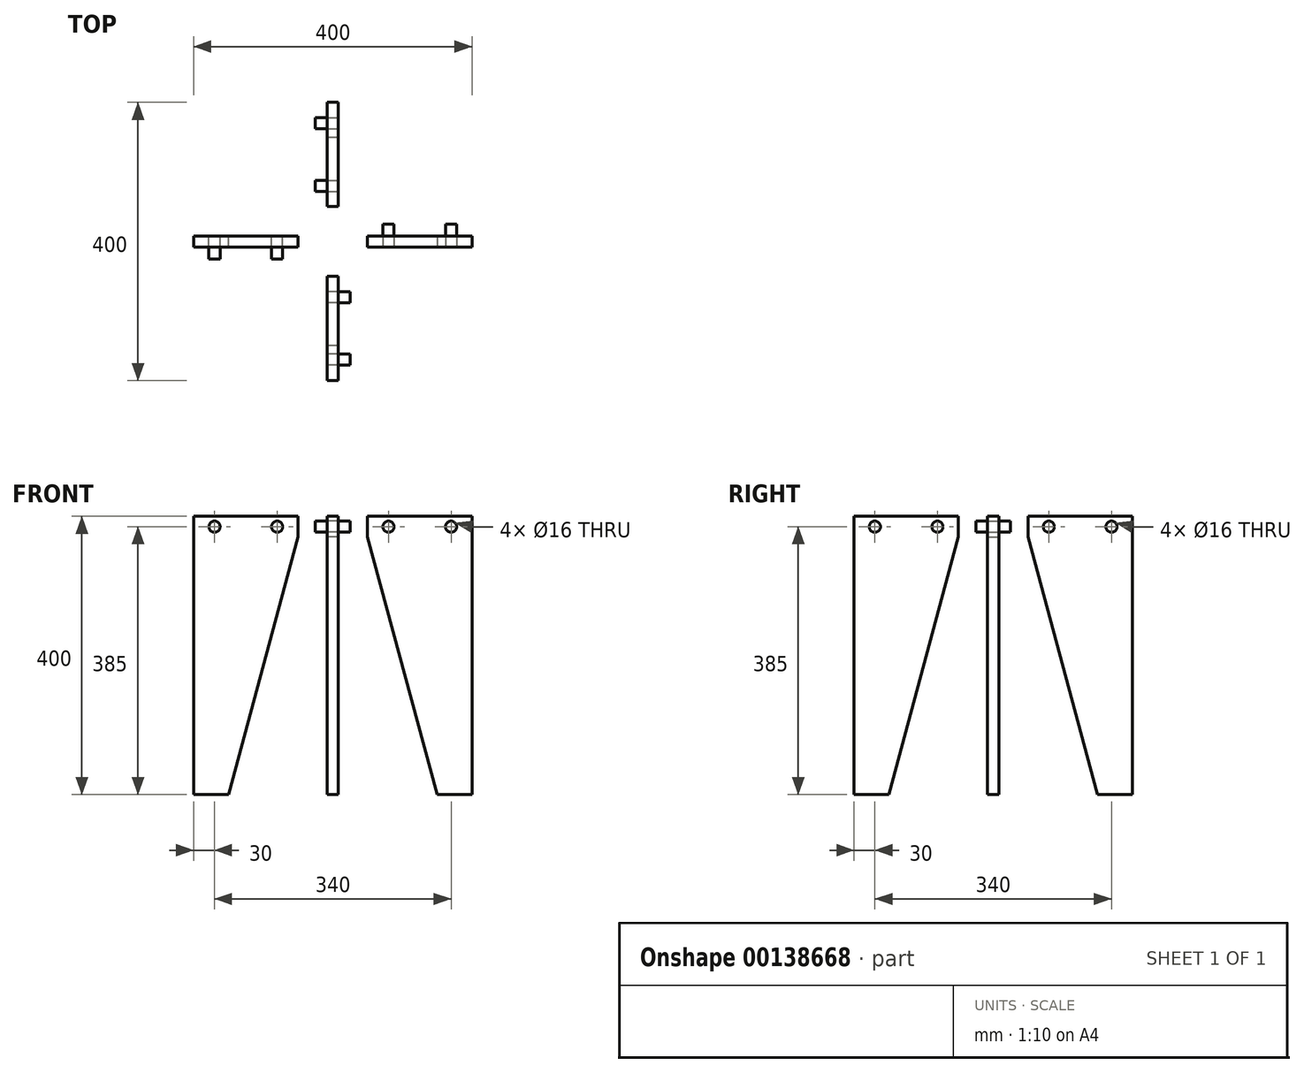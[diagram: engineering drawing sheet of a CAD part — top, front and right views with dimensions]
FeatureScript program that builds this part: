
annotation { "Feature Type Name" : "Feature", "Feature Type Description" : "" }
export const myFeature = defineFeature(function(context is Context, id is Id, definition is map)
    precondition{}
    {
        {
            var Q0;
            Q0=qCreatedBy(makeId("Front.planeOp"),FACE);
            var sketch = newSketch(context, id + "F0", { "sketchPlane" : qUnion([Q0])});
            skLineSegment(sketch, "E0", {"start": v(0, 0) * mm, "end": v(0, 319.28) * mm, "construction": true});
            skLineSegment(sketch, "E1", {"start": v(-50, 400) * mm, "end": v(-200, 400) * mm});
            skLineSegment(sketch, "E2", {"start": v(-200, 400) * mm, "end": v(-200, 0) * mm});
            skLineSegment(sketch, "E3", {"start": v(-200, 0) * mm, "end": v(-150, 0) * mm});
            skLineSegment(sketch, "E4.bottom", {"start": v(-250, 400) * mm, "end": v(0, 400) * mm, "construction": true});
            skLineSegment(sketch, "E4.top", {"start": v(-250, 370) * mm, "end": v(0, 370) * mm, "construction": true});
            skLineSegment(sketch, "E4.left", {"start": v(-250, 400) * mm, "end": v(-250, 370) * mm, "construction": true});
            skLineSegment(sketch, "E4.right", {"start": v(0, 400) * mm, "end": v(0, 370) * mm, "construction": true});
            skLineSegment(sketch, "E5", {"start": v(-50, 400) * mm, "end": v(-50, 370) * mm});
            skLineSegment(sketch, "E6", {"start": v(-50, 370) * mm, "end": v(-150, 0) * mm});
            skLineSegment(sketch, "E7", {"start": v(-80, 385) * mm, "end": v(-170, 385) * mm, "construction": true});
            skCircle(sketch, "E8", {"center": v(-80, 385) * mm, "radius": 8 * mm});
            skCircle(sketch, "E9", {"center": v(-170, 385) * mm, "radius": 8 * mm});
            skSolve(sketch);
        }
        {
            var Q0;
            {var subQ5=sQuery(id+"F0.wireOp",EDGE,"E5");Q0=makeQuery(id+"F0.imprint","IMPRINT",FACE,{"disambiguationData":[TD([[makeQuery(id+"F0.imprint","IMPRINT",EDGE,{"derivedFrom":subQ5}),-1.0]])]});}
            var Q1;
            {var subQ0=sQuery(id+"F0.wireOp",EDGE,"E3");Q1=makeQuery(id+"F0.imprint","IMPRINT",FACE,{"disambiguationData":[TD([[makeQuery(id+"F0.imprint","IMPRINT",EDGE,{"derivedFrom":subQ0}),1.0]])]});}
            extrude(context, id + "F1", {"entities" : qUnion([Q0, Q1]), "endBound" : BoundingType.SYMMETRIC, "depth" : 16 * mm});
        }
        {
            var Q0;
            Q0=makeQuery(id+"F0.imprint","IMPRINT",FACE,{"disambiguationData":[TD([[makeQuery(id+"F0.imprint","IMPRINT",EDGE,{"derivedFrom":sQuery(id+"F0.wireOp",EDGE,"E8")}),1.0]])]});
            var Q1;
            Q1=makeQuery(id+"F0.imprint","IMPRINT",FACE,{"disambiguationData":[TD([[makeQuery(id+"F0.imprint","IMPRINT",EDGE,{"derivedFrom":sQuery(id+"F0.wireOp",EDGE,"E9")}),1.0]])]});
            extrude(context, id + "F2", {"entities" : qUnion([Q0, Q1]), "endBound" : BoundingType.SYMMETRIC, "depth" : 50 * mm});
        }
        {
            var Q0;
            Q0=makeQuery(id+"F1.opExtrude","CAP_FACE",FACE,{"disambiguationData":[OSD([sQuery(id+"F0.wireOp",EDGE,"E2"),sQuery(id+"F0.wireOp",EDGE,"E3"),sQuery(id+"F0.wireOp",EDGE,"E4.bottom"),sQuery(id+"F0.wireOp",EDGE,"E5"),sQuery(id+"F0.wireOp",EDGE,"E6")])],"isStart":false});
            var sketch = newSketch(context, id + "F3", { "sketchPlane" : qUnion([Q0])});
            skLineSegment(sketch, "E10", {"start": v(-170, 385) * mm, "end": v(-80, 385) * mm, "construction": true});
            skCircle(sketch, "E11", {"center": v(-170, 385) * mm, "radius": 8 * mm});
            skCircle(sketch, "E12", {"center": v(-80, 385) * mm, "radius": 8 * mm});
            skSolve(sketch);
        }
        {
            var Q0;
            Q0=makeQuery(id+"F3.imprint","IMPRINT",FACE,{"disambiguationData":[TD([[makeQuery(id+"F3.imprint","IMPRINT",EDGE,{"derivedFrom":sQuery(id+"F3.wireOp",EDGE,"E11")}),1.0]])]});
            var Q1;
            Q1=makeQuery(id+"F3.imprint","IMPRINT",FACE,{"disambiguationData":[TD([[makeQuery(id+"F3.imprint","IMPRINT",EDGE,{"derivedFrom":sQuery(id+"F3.wireOp",EDGE,"E12")}),1.0]])]});
            extrude(context, id + "F4", {"entities" : qUnion([Q0, Q1]), "operationType" : NewBodyOperationType.REMOVE, "endBound" : BoundingType.THROUGH_ALL, "oppositeDirection" : true, "depth" : 25 * mm});
        }
        {
            var Q0;
            Q0=makeQuery(id+"F1.opExtrude","SWEPT_BODY",BODY,{"disambiguationData":[OSD([sQuery(id+"F0.wireOp",EDGE,"E2"),sQuery(id+"F0.wireOp",EDGE,"E3"),sQuery(id+"F0.wireOp",EDGE,"E4.bottom"),sQuery(id+"F0.wireOp",EDGE,"E5"),sQuery(id+"F0.wireOp",EDGE,"E6")])]});
            var Q1;
            Q1=makeQuery(id+"F2.opExtrude","SWEPT_BODY",BODY,{"disambiguationData":[OSD([sQuery(id+"F0.wireOp",EDGE,"E8")])]});
            var Q2;
            Q2=makeQuery(id+"F2.opExtrude","SWEPT_BODY",BODY,{"disambiguationData":[OSD([sQuery(id+"F0.wireOp",EDGE,"E9")])]});
            var Q3;
            Q3=sQuery(id+"F0.wireOp",EDGE,"E0");
            circularPattern(context, id + "F5", {"entities" : qUnion([Q0, Q1, Q2]), "axis" : qUnion([Q3]), "angle" : 90 * degree, "instanceCount" : 4});
        }
    });
